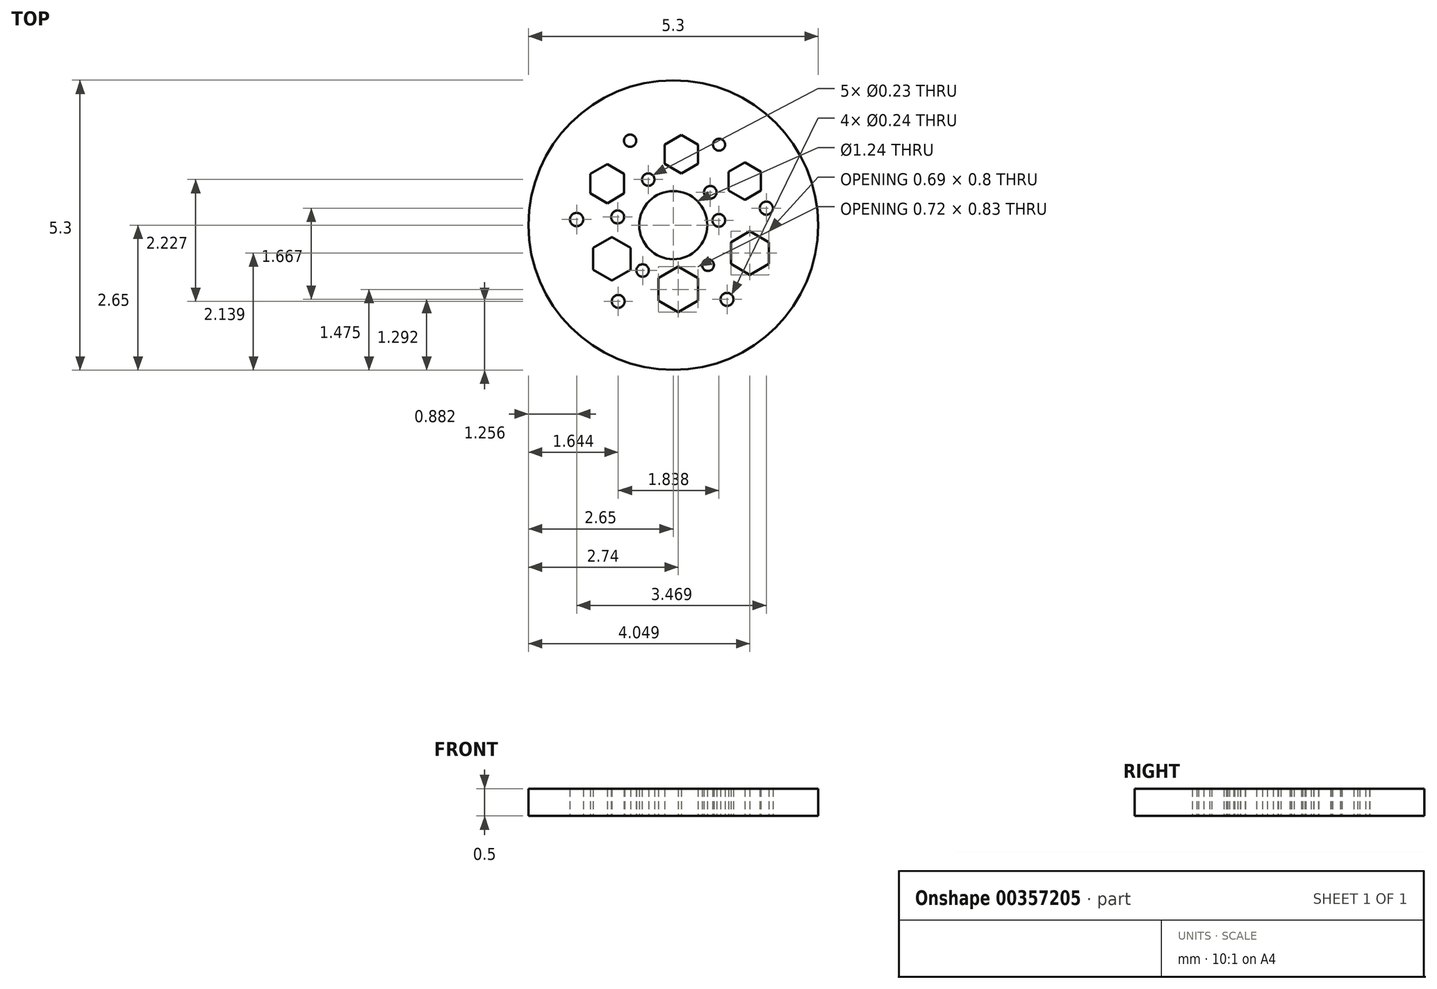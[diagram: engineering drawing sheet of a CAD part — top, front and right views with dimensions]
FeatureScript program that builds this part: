
annotation { "Feature Type Name" : "Feature", "Feature Type Description" : "" }
export const myFeature = defineFeature(function(context is Context, id is Id, definition is map)
    precondition{}
    {
        {
            var Q0;
            Q0=qCreatedBy(makeId("Top.planeOp"),FACE);
            var sketch = newSketch(context, id + "F0", { "sketchPlane" : qUnion([Q0])});
            skCircle(sketch, "E0", {"center": v(0, 0) * mm, "radius": 0.62 * mm});
            skCircle(sketch, "E1", {"center": v(0, 0) * mm, "radius": 2.07 * mm});
            skCircle(sketch, "E2", {"center": v(0, 0) * mm, "radius": 2.65 * mm});
            skPoint(sketch, "E3.0.midPoint", {"position": v(-0.96, 0.87) * mm});
            skPoint(sketch, "E4.0.midPoint", {"position": v(0.34, 1.3) * mm});
            skPoint(sketch, "E5.0.midPoint", {"position": v(1.42, 0.59) * mm});
            skPoint(sketch, "E6.0.midPoint", {"position": v(0.4, -1.33) * mm});
            skPoint(sketch, "E7.0.midPoint", {"position": v(-0.9, -0.59) * mm});
            skPoint(sketch, "E8.0.midPoint", {"position": v(1.64, -0.59) * mm});
            skPoint(sketch, "E9.0.midPoint", {"position": v(-1.18, -0.69) * mm});
            skPoint(sketch, "E10.0.midPoint", {"position": v(0.14, -1.4) * mm});
            skPoint(sketch, "E11.0.midPoint", {"position": v(1.3, -0.73) * mm});
            skPoint(sketch, "E12.0.midPoint", {"position": v(1.3, 0.8) * mm});
            skPoint(sketch, "E13.0.midPoint", {"position": v(0.1, 1.23) * mm});
            skPoint(sketch, "E14.0.midPoint", {"position": v(-1.2, 0.76) * mm});
            skPoint(sketch, "E15.orphan", {"position": v(-1.14, 1.18) * mm});
            skPoint(sketch, "E16.orphan", {"position": v(-0.96, 1) * mm});
            skPoint(sketch, "E3.1.start.orphan", {"position": v(-0.96, 0.74) * mm});
            skPoint(sketch, "E17.orphan", {"position": v(-1.14, 0.56) * mm});
            skPoint(sketch, "E18.orphan", {"position": v(-1.4, 0.56) * mm});
            skPoint(sketch, "E19.orphan", {"position": v(-1.58, 0.74) * mm});
            skPoint(sketch, "E3.cCircle.center.orphan", {"position": v(-1.27, 0.87) * mm});
            skPoint(sketch, "E14.0.end.orphan", {"position": v(-1.27, 0.72) * mm});
            skPoint(sketch, "E14.5.end.orphan", {"position": v(-1.14, 0.8) * mm});
            skPoint(sketch, "E20.orphan", {"position": v(-1.3, -0.12) * mm});
            skPoint(sketch, "E21.orphan", {"position": v(-0.9, -0.36) * mm});
            skPoint(sketch, "E7.0.end.orphan", {"position": v(-0.9, -0.82) * mm});
            skPoint(sketch, "E9.cCircle.center.orphan", {"position": v(-1.3, -0.59) * mm});
            skPoint(sketch, "E22.orphan", {"position": v(-1.24, -0.75) * mm});
            skPoint(sketch, "E23.orphan", {"position": v(-1.12, -0.62) * mm});
            skPoint(sketch, "E24.orphan", {"position": v(0, -0.87) * mm});
            skPoint(sketch, "E25.orphan", {"position": v(0.4, -1.1) * mm});
            skPoint(sketch, "E26.orphan", {"position": v(0.4, -1.56) * mm});
            skPoint(sketch, "E27.orphan", {"position": v(0.1, -1.17) * mm});
            skPoint(sketch, "E10.cCircle.center.orphan", {"position": v(0, -1.33) * mm});
            skPoint(sketch, "E28.orphan", {"position": v(0.1, -1.49) * mm});
            skPoint(sketch, "E10.0.start.orphan", {"position": v(0.18, -1.33) * mm});
            skPoint(sketch, "E29.orphan", {"position": v(0.34, 1.18) * mm});
            skPoint(sketch, "E4.0.start.orphan", {"position": v(0.34, 1.42) * mm});
            skPoint(sketch, "E30.orphan", {"position": v(-0.07, 1.43) * mm});
            skPoint(sketch, "E13.0.start.orphan", {"position": v(0.15, 1.3) * mm});
            skPoint(sketch, "E31.orphan", {"position": v(0.07, 1.17) * mm});
            skPoint(sketch, "E32.orphan", {"position": v(-0.08, 1.18) * mm});
            skPoint(sketch, "E13.cCircle.center.orphan", {"position": v(0, 1.3) * mm});
            skPoint(sketch, "E33.orphan", {"position": v(1.22, 1.24) * mm});
            skPoint(sketch, "E34.orphan", {"position": v(1.46, 1.15) * mm});
            skPoint(sketch, "E35.orphan", {"position": v(1.53, 0.67) * mm});
            skPoint(sketch, "E36.orphan", {"position": v(1.32, 0.5) * mm});
            skPoint(sketch, "E37.orphan", {"position": v(1.07, 0.52) * mm});
            skPoint(sketch, "E38.orphan", {"position": v(1.14, 0.99) * mm});
            skPoint(sketch, "E12.cCircle.center.orphan", {"position": v(1.2, 0.87) * mm});
            skPoint(sketch, "E39.orphan", {"position": v(1.27, 0.75) * mm});
            skPoint(sketch, "E12.0.start.orphan", {"position": v(1.34, 0.86) * mm});
            skPoint(sketch, "E40.orphan", {"position": v(1.34, -0.15) * mm});
            skPoint(sketch, "E41.orphan", {"position": v(1.64, -0.78) * mm});
            skPoint(sketch, "E8.6.end.orphan", {"position": v(1.64, -0.4) * mm});
            skPoint(sketch, "E42.orphan", {"position": v(1.1, -0.49) * mm});
            skPoint(sketch, "E43.orphan", {"position": v(1.25, -0.41) * mm});
            skPoint(sketch, "E44.orphan", {"position": v(1.4, -0.51) * mm});
            skPoint(sketch, "E11.1.start.orphan", {"position": v(1.23, -0.77) * mm});
            skPoint(sketch, "E11.5.end.orphan", {"position": v(1.39, -0.69) * mm});
            skPoint(sketch, "E11.cCircle.center.orphan", {"position": v(1.24, -0.59) * mm});
            skCircle(sketch, "E45.cCircle", {"center": v(-1.2, 0.76) * mm, "radius": 0.3 * mm, "construction": true});
            skLineSegment(sketch, "E45.0", {"start": v(-0.9, 0.94) * mm, "end": v(-0.9, 0.58) * mm});
            skLineSegment(sketch, "E45.1", {"start": v(-0.9, 0.58) * mm, "end": v(-1.2, 0.4) * mm});
            skLineSegment(sketch, "E45.2", {"start": v(-1.2, 0.4) * mm, "end": v(-1.52, 0.58) * mm});
            skLineSegment(sketch, "E45.3", {"start": v(-1.52, 0.58) * mm, "end": v(-1.52, 0.94) * mm});
            skLineSegment(sketch, "E45.4", {"start": v(-1.52, 0.94) * mm, "end": v(-1.2, 1.11) * mm});
            skLineSegment(sketch, "E45.5", {"start": v(-1.2, 1.11) * mm, "end": v(-0.9, 0.94) * mm});
            skPoint(sketch, "E45.0.midPoint", {"position": v(-0.9, 0.76) * mm});
            skCircle(sketch, "E46.cCircle", {"center": v(0.15, 1.3) * mm, "radius": 0.3 * mm, "construction": true});
            skLineSegment(sketch, "E46.0", {"start": v(0.45, 1.47) * mm, "end": v(0.45, 1.12) * mm});
            skLineSegment(sketch, "E46.1", {"start": v(0.45, 1.12) * mm, "end": v(0.15, 0.94) * mm});
            skLineSegment(sketch, "E46.2", {"start": v(0.15, 0.94) * mm, "end": v(-0.16, 1.12) * mm});
            skLineSegment(sketch, "E46.3", {"start": v(-0.16, 1.12) * mm, "end": v(-0.16, 1.47) * mm});
            skLineSegment(sketch, "E46.4", {"start": v(-0.16, 1.47) * mm, "end": v(0.15, 1.65) * mm});
            skLineSegment(sketch, "E46.5", {"start": v(0.15, 1.65) * mm, "end": v(0.45, 1.47) * mm});
            skPoint(sketch, "E46.0.midPoint", {"position": v(0.45, 1.3) * mm});
            skCircle(sketch, "E47.cCircle", {"center": v(1.3, 0.8) * mm, "radius": 0.3 * mm, "construction": true});
            skLineSegment(sketch, "E47.0", {"start": v(1.6, 0.97) * mm, "end": v(1.6, 0.63) * mm});
            skLineSegment(sketch, "E47.1", {"start": v(1.6, 0.63) * mm, "end": v(1.3, 0.46) * mm});
            skLineSegment(sketch, "E47.2", {"start": v(1.3, 0.46) * mm, "end": v(1.01, 0.63) * mm});
            skLineSegment(sketch, "E47.3", {"start": v(1.01, 0.63) * mm, "end": v(1.01, 0.97) * mm});
            skLineSegment(sketch, "E47.4", {"start": v(1.01, 0.97) * mm, "end": v(1.3, 1.14) * mm});
            skLineSegment(sketch, "E47.5", {"start": v(1.3, 1.14) * mm, "end": v(1.6, 0.97) * mm});
            skPoint(sketch, "E47.0.midPoint", {"position": v(1.6, 0.8) * mm});
            skCircle(sketch, "E48.cCircle", {"center": v(-1.12, -0.62) * mm, "radius": 0.34 * mm, "construction": true});
            skLineSegment(sketch, "E48.0", {"start": v(-0.78, -0.42) * mm, "end": v(-0.78, -0.82) * mm});
            skLineSegment(sketch, "E48.1", {"start": v(-0.78, -0.82) * mm, "end": v(-1.12, -1.01) * mm});
            skLineSegment(sketch, "E48.2", {"start": v(-1.12, -1.01) * mm, "end": v(-1.47, -0.82) * mm});
            skLineSegment(sketch, "E48.3", {"start": v(-1.47, -0.82) * mm, "end": v(-1.47, -0.42) * mm});
            skLineSegment(sketch, "E48.4", {"start": v(-1.47, -0.42) * mm, "end": v(-1.12, -0.22) * mm});
            skLineSegment(sketch, "E48.5", {"start": v(-1.12, -0.22) * mm, "end": v(-0.78, -0.42) * mm});
            skPoint(sketch, "E48.0.midPoint", {"position": v(-0.78, -0.62) * mm});
            skCircle(sketch, "E49.cCircle", {"center": v(0.1, -1.17) * mm, "radius": 0.36 * mm, "construction": true});
            skLineSegment(sketch, "E49.0", {"start": v(0.45, -0.97) * mm, "end": v(0.45, -1.38) * mm});
            skLineSegment(sketch, "E49.1", {"start": v(0.45, -1.38) * mm, "end": v(0.1, -1.6) * mm});
            skLineSegment(sketch, "E49.2", {"start": v(0.1, -1.6) * mm, "end": v(-0.27, -1.38) * mm});
            skLineSegment(sketch, "E49.3", {"start": v(-0.27, -1.38) * mm, "end": v(-0.27, -0.97) * mm});
            skLineSegment(sketch, "E49.4", {"start": v(-0.27, -0.97) * mm, "end": v(0.1, -0.76) * mm});
            skLineSegment(sketch, "E49.5", {"start": v(0.1, -0.76) * mm, "end": v(0.45, -0.97) * mm});
            skPoint(sketch, "E49.0.midPoint", {"position": v(0.45, -1.17) * mm});
            skCircle(sketch, "E50.cCircle", {"center": v(1.4, -0.51) * mm, "radius": 0.35 * mm, "construction": true});
            skLineSegment(sketch, "E50.0", {"start": v(1.74, -0.31) * mm, "end": v(1.74, -0.71) * mm});
            skLineSegment(sketch, "E50.1", {"start": v(1.74, -0.71) * mm, "end": v(1.4, -0.9) * mm});
            skLineSegment(sketch, "E50.2", {"start": v(1.4, -0.9) * mm, "end": v(1.05, -0.71) * mm});
            skLineSegment(sketch, "E50.3", {"start": v(1.05, -0.71) * mm, "end": v(1.05, -0.31) * mm});
            skLineSegment(sketch, "E50.4", {"start": v(1.05, -0.31) * mm, "end": v(1.4, -0.11) * mm});
            skLineSegment(sketch, "E50.5", {"start": v(1.4, -0.11) * mm, "end": v(1.74, -0.31) * mm});
            skPoint(sketch, "E50.0.midPoint", {"position": v(1.74, -0.51) * mm});
            skCircle(sketch, "E51", {"center": v(-1.02, 0.15) * mm, "radius": 0.12 * mm});
            skCircle(sketch, "E52", {"center": v(-0.46, 0.83) * mm, "radius": 0.11 * mm});
            skCircle(sketch, "E53", {"center": v(0.68, 0.6) * mm, "radius": 0.11 * mm});
            skCircle(sketch, "E54", {"center": v(-0.56, -0.83) * mm, "radius": 0.11 * mm});
            skCircle(sketch, "E55", {"center": v(0.64, -0.73) * mm, "radius": 0.1 * mm});
            skCircle(sketch, "E56", {"center": v(0.84, 1.47) * mm, "radius": 0.1 * mm});
            skCircle(sketch, "E57", {"center": v(-0.79, 1.54) * mm, "radius": 0.11 * mm});
            skCircle(sketch, "E58", {"center": v(-1.77, 0.1) * mm, "radius": 0.12 * mm});
            skCircle(sketch, "E59", {"center": v(-1, -1.4) * mm, "radius": 0.12 * mm});
            skCircle(sketch, "E60", {"center": v(0.98, -1.36) * mm, "radius": 0.12 * mm});
            skCircle(sketch, "E61", {"center": v(0.83, 0.09) * mm, "radius": 0.12 * mm});
            skCircle(sketch, "E62", {"center": v(1.7, 0.3) * mm, "radius": 0.12 * mm});
            skSolve(sketch);
        }
        {
            var Q0;
            Q0=makeQuery(id+"F0.imprint","IMPRINT",FACE,{"disambiguationData":[TD([[makeQuery(id+"F0.imprint","IMPRINT",EDGE,{"derivedFrom":sQuery(id+"F0.wireOp",EDGE,"E0")}),-1.0]])]});
            var Q1;
            Q1=makeQuery(id+"F0.imprint","IMPRINT",FACE,{"disambiguationData":[TD([[makeQuery(id+"F0.imprint","IMPRINT",EDGE,{"derivedFrom":sQuery(id+"F0.wireOp",EDGE,"E1")}),-1.0]])]});
            extrude(context, id + "F1", {"entities" : qUnion([Q0, Q1]), "depth" : .5 * mm});
        }
    });
